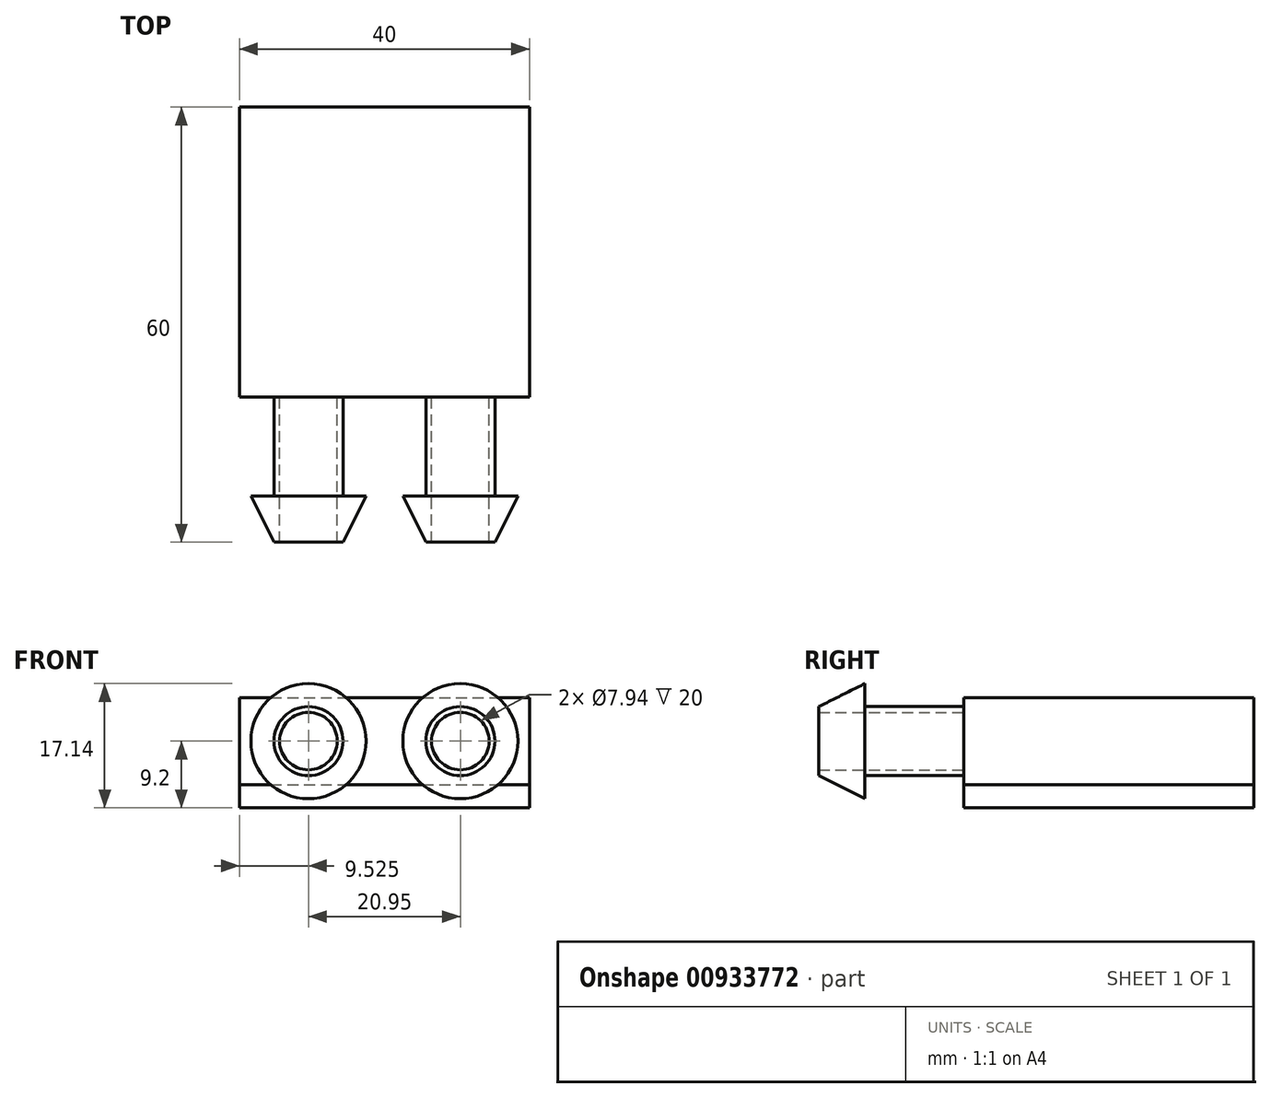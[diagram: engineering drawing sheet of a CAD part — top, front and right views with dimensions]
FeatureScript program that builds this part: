
annotation { "Feature Type Name" : "Feature", "Feature Type Description" : "" }
export const myFeature = defineFeature(function(context is Context, id is Id, definition is map)
    precondition{}
    {
        {
            var Q0;
            Q0=qCreatedBy(makeId("Top.planeOp"),FACE);
            var sketch = newSketch(context, id + "F0", { "sketchPlane" : qUnion([Q0])});
            skLineSegment(sketch, "E0.bottom", {"start": v(0, 0) * mm, "end": v(40, 0) * mm});
            skLineSegment(sketch, "E0.top", {"start": v(0, 40) * mm, "end": v(40, 40) * mm});
            skLineSegment(sketch, "E0.left", {"start": v(0, 0) * mm, "end": v(0, 40) * mm});
            skLineSegment(sketch, "E0.right", {"start": v(40, 0) * mm, "end": v(40, 40) * mm});
            skSolve(sketch);
        }
        {
            var Q0;
            Q0=makeQuery(id+"F0.imprint","IMPRINT",FACE,{"disambiguationData":[TD([[makeQuery(id+"F0.imprint","IMPRINT",EDGE,{"derivedFrom":sQuery(id+"F0.wireOp",EDGE,"E0.bottom")}),1.0]])]});
            extrude(context, id + "F1", {"entities" : qUnion([Q0]), "depth" : 3.2 * mm, "offsetDistance" : 25.4 * mm});
        }
        {
            var Q0;
            Q0=makeQuery(id+"F1.opExtrude","CAP_FACE",FACE,{"disambiguationData":[OSD([sQuery(id+"F0.wireOp",EDGE,"E0.bottom"),sQuery(id+"F0.wireOp",EDGE,"E0.top"),sQuery(id+"F0.wireOp",EDGE,"E0.left"),sQuery(id+"F0.wireOp",EDGE,"E0.right")])],"isStart":false});
            var sketch = newSketch(context, id + "F2", { "sketchPlane" : qUnion([Q0])});
            skLineSegment(sketch, "E1.bottom", {"start": v(0, 40) * mm, "end": v(40, 40) * mm});
            skLineSegment(sketch, "E1.top", {"start": v(0, 0) * mm, "end": v(40, 0) * mm});
            skLineSegment(sketch, "E1.left", {"start": v(0, 40) * mm, "end": v(0, 0) * mm});
            skLineSegment(sketch, "E1.right", {"start": v(40, 40) * mm, "end": v(40, 0) * mm});
            skSolve(sketch);
        }
        {
            var Q0;
            Q0 = qSketchRegion(id + "F2", true);
            extrude(context, id + "F3", {"entities" : qUnion([Q0]), "depth" : 12 * mm, "offsetDistance" : 25.4 * mm});
        }
        {
            var Q0;
            Q0=makeQuery(id+"F3.opExtrude","SWEPT_FACE",FACE,{"disambiguationData":[OSD([sQuery(id+"F2.wireOp",EDGE,"E1.top")])]});
            var sketch = newSketch(context, id + "F4", { "sketchPlane" : qUnion([Q0])});
            skCircle(sketch, "E2", {"center": v(9.53, 9.2) * mm, "radius": 4.76 * mm});
            skCircle(sketch, "E3", {"center": v(30.48, 9.2) * mm, "radius": 4.76 * mm});
            skPoint(sketch, "E4", {"position": v(0, 9.2) * mm});
            skPoint(sketch, "E5", {"position": v(4.76, 9.2) * mm});
            skPoint(sketch, "E6", {"position": v(35.24, 9.2) * mm});
            skSolve(sketch);
        }
        {
            var Q0;
            Q0 = qSketchRegion(id + "F4", true);
            extrude(context, id + "F5", {"entities" : qUnion([Q0]), "operationType" : NewBodyOperationType.ADD, "depth" : 20 * mm, "offsetDistance" : 25.4 * mm});
        }
        {
            var Q0;
            Q0=makeQuery(id+"F3.opExtrude","SWEPT_EDGE",EDGE,{"disambiguationData":[OSD([sQuery(id+"F2.wireOp",EDGE,"E1.top"),sQuery(id+"F2.wireOp",EDGE,"E1.right")])]});
            cPoint(context, id + "F6", {"entities" : qUnion([Q0]), "parameter" : 0.5});
        }
        {
            var Q0;
            Q0=makeQuery(id+"F3.opExtrude","SWEPT_EDGE",EDGE,{"disambiguationData":[OSD([sQuery(id+"F2.wireOp",EDGE,"E1.bottom"),sQuery(id+"F2.wireOp",EDGE,"E1.right")])]});
            cPoint(context, id + "F7", {"entities" : qUnion([Q0]), "parameter" : 0.5});
        }
        {
            var Q0;
            Q0=makeQuery(id+"F3.opExtrude","SWEPT_EDGE",EDGE,{"disambiguationData":[OSD([sQuery(id+"F2.wireOp",EDGE,"E1.top"),sQuery(id+"F2.wireOp",EDGE,"E1.left")])]});
            cPoint(context, id + "F8", {"entities" : qUnion([Q0]), "parameter" : 0.5});
        }
        {
            var Q0;
            Q0 = qCreatedBy(id + "F6" ,VERTEX);
            var Q1;
            Q1 = qCreatedBy(id + "F7" ,VERTEX);
            var Q2;
            Q2 = qCreatedBy(id + "F8" ,VERTEX);
            cPlane(context, id + "F9", {"entities" : qUnion([Q0, Q1, Q2]), "cplaneType" : CPlaneType.THREE_POINT, "offset" : 25.4 * mm, "width" : 152.4 * mm, "height" : 152.4 * mm});
        }
        {
            var Q0;
            Q0=qCreatedBy(id+"F9.planeOp",FACE);
            var sketch = newSketch(context, id + "F10", { "sketchPlane" : qUnion([Q0])});
            skLineSegment(sketch, "E7", {"start": v(4.76, 20) * mm, "end": v(1.59, 13.65) * mm});
            skLineSegment(sketch, "E8", {"start": v(1.59, 13.65) * mm, "end": v(4.76, 13.65) * mm});
            skLineSegment(sketch, "E9", {"start": v(4.76, 13.65) * mm, "end": v(4.76, 20) * mm});
            skLineSegment(sketch, "E10", {"start": v(35.24, 20) * mm, "end": v(35.24, 13.65) * mm});
            skLineSegment(sketch, "E11", {"start": v(35.24, 13.65) * mm, "end": v(38.41, 13.65) * mm});
            skLineSegment(sketch, "E12", {"start": v(38.41, 13.65) * mm, "end": v(35.24, 20) * mm});
            skSolve(sketch);
        }
        {
            var Q0;
            Q0=makeQuery(id+"F10.imprint","IMPRINT",FACE,{"disambiguationData":[TD([[makeQuery(id+"F10.imprint","IMPRINT",EDGE,{"derivedFrom":sQuery(id+"F10.wireOp",EDGE,"E7")}),1.0]])]});
            var Q1;
            Q1=makeQuery(id+"F5.opExtrude","CAP_EDGE",EDGE,{"disambiguationData":[OSD([sQuery(id+"F4.wireOp",EDGE,"E2")])],"isStart":false});
            revolve(context, id + "F11", {"operationType" : NewBodyOperationType.ADD, "surfaceOperationType" : NewSurfaceOperationType.NEW, "entities" : qUnion([Q0]), "axis" : qUnion([Q1]), "revolveType" : RevolveType.FULL});
        }
        {
            var Q0;
            Q0=makeQuery(id+"F10.imprint","IMPRINT",FACE,{"disambiguationData":[TD([[makeQuery(id+"F10.imprint","IMPRINT",EDGE,{"derivedFrom":sQuery(id+"F10.wireOp",EDGE,"E10")}),1.0]])]});
            var Q1;
            Q1=makeQuery(id+"F5.opExtrude","CAP_EDGE",EDGE,{"disambiguationData":[OSD([sQuery(id+"F4.wireOp",EDGE,"E3")])],"isStart":false});
            revolve(context, id + "F12", {"operationType" : NewBodyOperationType.ADD, "surfaceOperationType" : NewSurfaceOperationType.NEW, "entities" : qUnion([Q0]), "axis" : qUnion([Q1]), "revolveType" : RevolveType.FULL});
        }
        {
            var Q0;
            Q0=sQuery(id+"F4.wireOp",VERTEX,"E2.center");
            var Q1;
            Q1=sQuery(id+"F4.wireOp",VERTEX,"E3.center");
            var Q2;
            Q2=makeQuery(id+"F3.opExtrude","SWEPT_BODY",BODY,{"disambiguationData":[OSD([sQuery(id+"F2.wireOp",EDGE,"E1.bottom"),sQuery(id+"F2.wireOp",EDGE,"E1.top"),sQuery(id+"F2.wireOp",EDGE,"E1.left"),sQuery(id+"F2.wireOp",EDGE,"E1.right")])]});
            hole(context, id + "F13", {"style" : HoleStyle.SIMPLE, "endStyle" : HoleEndStyle.THROUGH, "oppositeDirection" : true, "standardTappedOrClearance" : lookupTablePath({ "standard" : "ANSI", "engagement" : "75%", "pitch" : "16 tpi", "size" : "3/8", "type" : "Tapped" }), "standardBlindInLast" : lookupTablePath({ "standard" : "ANSI", "fit" : "Normal", "engagement" : "75%", "pitch" : "16 tpi", "size" : "3/8", "type" : "Clearance & tapped" }), "holeDiameter" : 7.94 * mm, "majorDiameter" : 9.52 * mm, "showTappedDepth" : true, "isTappedThrough" : true, "tappedDepth" : 10.8 * mm, "tapClearance" : 3, "locations" : qUnion([Q0, Q1]), "scope" : qUnion([Q2])});
        }
    });
